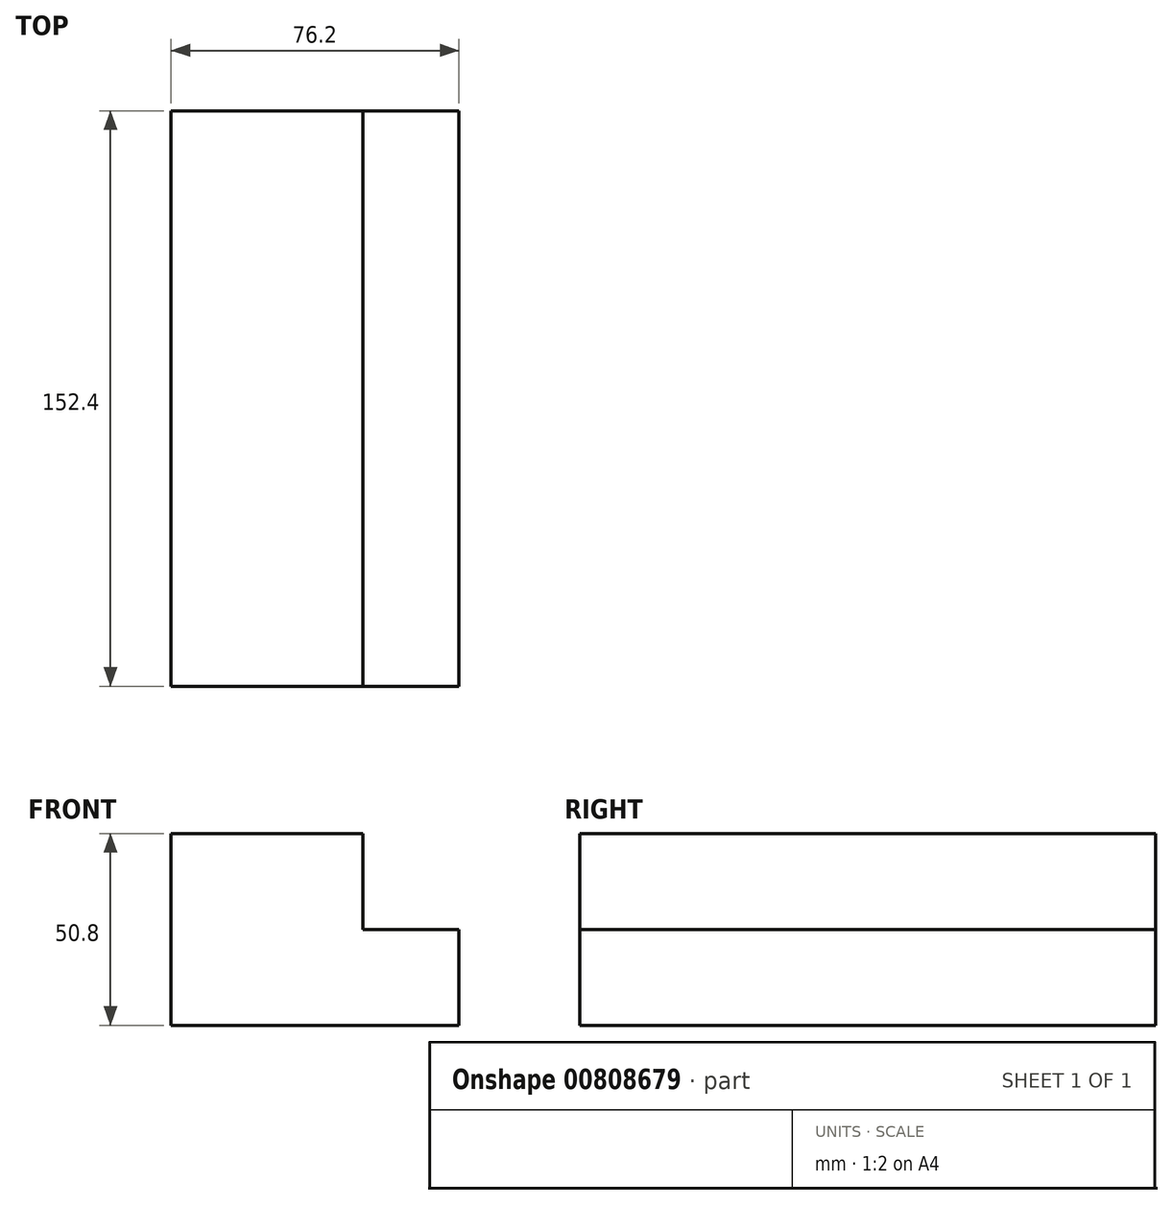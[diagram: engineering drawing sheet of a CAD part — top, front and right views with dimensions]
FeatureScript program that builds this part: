
annotation { "Feature Type Name" : "Feature", "Feature Type Description" : "" }
export const myFeature = defineFeature(function(context is Context, id is Id, definition is map)
    precondition{}
    {
        {
            var Q0;
            Q0=qCreatedBy(makeId("Front.planeOp"),FACE);
            var sketch = newSketch(context, id + "F0", { "sketchPlane" : qUnion([Q0])});
            skLineSegment(sketch, "E0.bottom", {"start": v(-66.84, 50.8) * mm, "end": v(-16.04, 50.8) * mm});
            skLineSegment(sketch, "E0.top", {"start": v(-66.84, 0) * mm, "end": v(-16.04, 0) * mm});
            skLineSegment(sketch, "E0.left", {"start": v(-66.84, 50.8) * mm, "end": v(-66.84, 0) * mm});
            skLineSegment(sketch, "E0.right", {"start": v(-16.04, 50.8) * mm, "end": v(-16.04, 0) * mm});
            skLineSegment(sketch, "E1.bottom", {"start": v(-16.04, 25.4) * mm, "end": v(9.36, 25.4) * mm});
            skLineSegment(sketch, "E1.top", {"start": v(-16.04, 0) * mm, "end": v(9.36, 0) * mm});
            skLineSegment(sketch, "E1.left", {"start": v(-16.04, 25.4) * mm, "end": v(-16.04, 0) * mm});
            skLineSegment(sketch, "E1.right", {"start": v(9.36, 25.4) * mm, "end": v(9.36, 0) * mm});
            skSolve(sketch);
        }
        {
            var Q0;
            Q0 = qSketchRegion(id + "F0", true);
            extrude(context, id + "F1", {"entities" : qUnion([Q0]), "depth" : 152.4 * mm, "offsetDistance" : 25.4 * mm});
        }
    });
